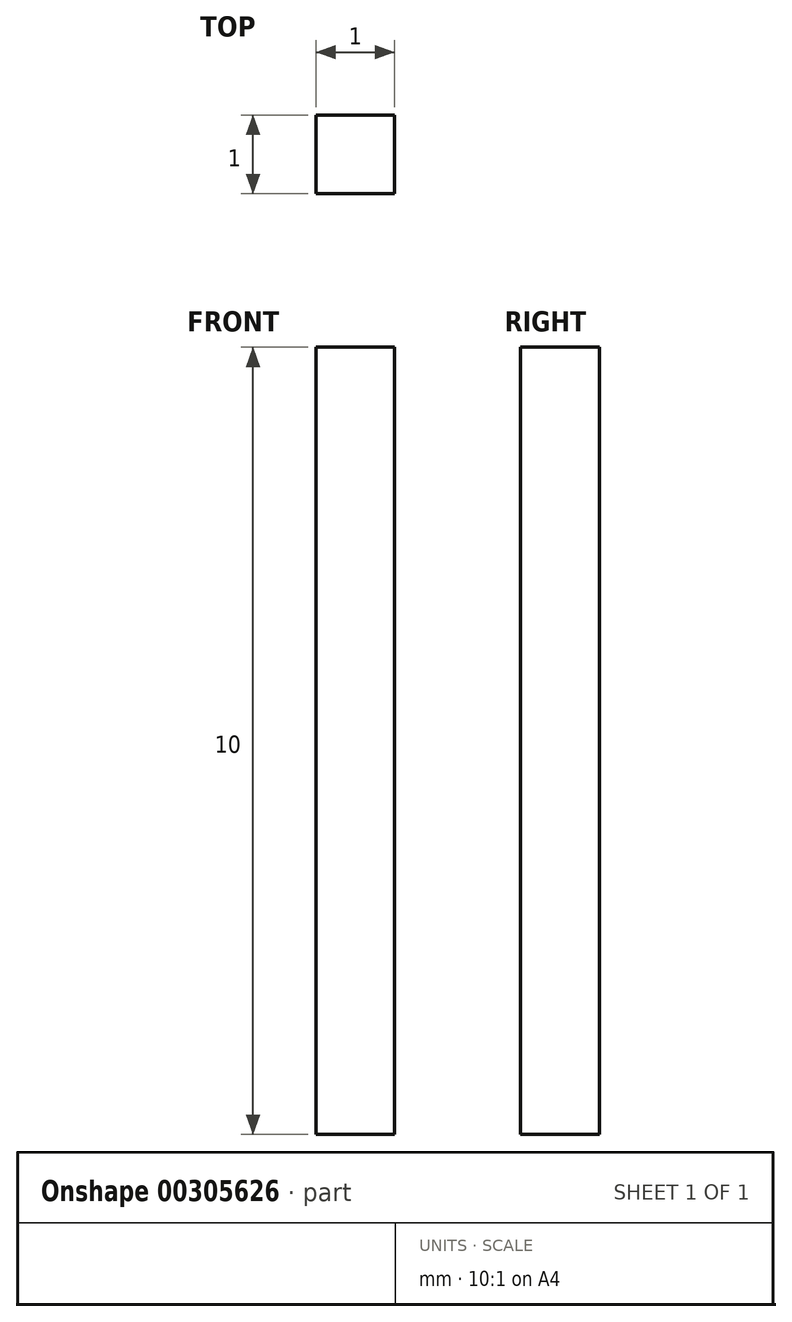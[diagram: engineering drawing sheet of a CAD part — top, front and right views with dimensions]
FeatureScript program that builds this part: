
annotation { "Feature Type Name" : "Feature", "Feature Type Description" : "" }
export const myFeature = defineFeature(function(context is Context, id is Id, definition is map)
    precondition{}
    {
        {
            var Q0;
            Q0=qCreatedBy(makeId("Top.planeOp"),FACE);
            var sketch = newSketch(context, id + "F0", { "sketchPlane" : qUnion([Q0])});
            skLineSegment(sketch, "E0.bottom", {"start": v(-0.5, -0.5) * mm, "end": v(0.5, -0.5) * mm});
            skLineSegment(sketch, "E0.top", {"start": v(-0.5, 0.5) * mm, "end": v(0.5, 0.5) * mm});
            skLineSegment(sketch, "E0.left", {"start": v(-0.5, -0.5) * mm, "end": v(-0.5, 0.5) * mm});
            skLineSegment(sketch, "E0.right", {"start": v(0.5, -0.5) * mm, "end": v(0.5, 0.5) * mm});
            skPoint(sketch, "E0.middle", {"position": v(0, 0) * mm});
            skSolve(sketch);
        }
        {
            var Q0;
            Q0 = qSketchRegion(id + "F0", true);
            extrude(context, id + "F1", {"entities" : qUnion([Q0]), "depth" : 10 * mm});
        }
    });
